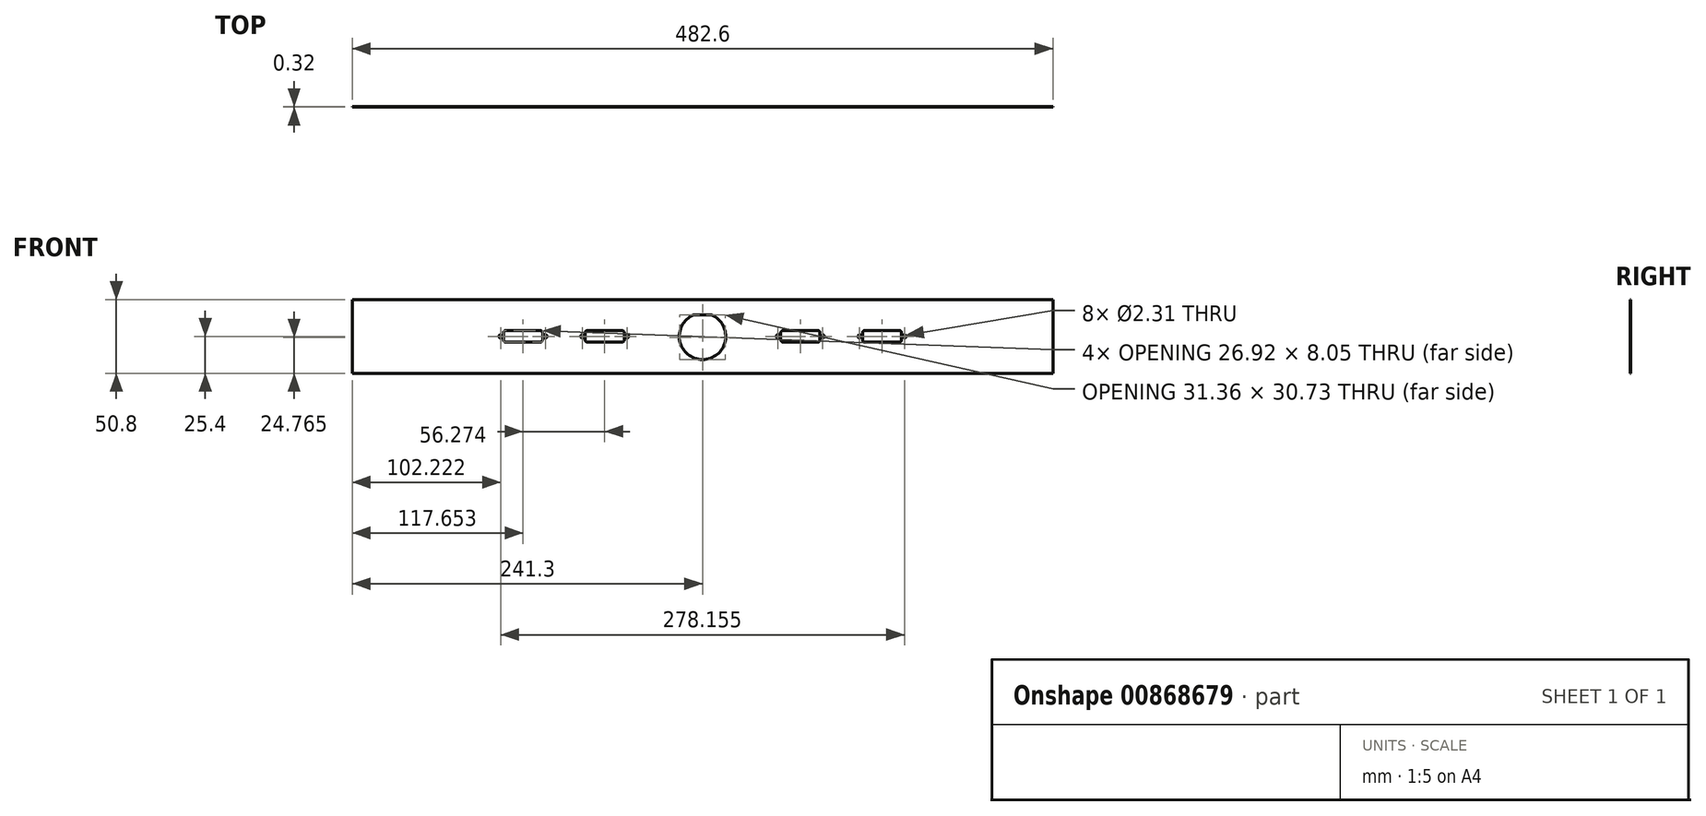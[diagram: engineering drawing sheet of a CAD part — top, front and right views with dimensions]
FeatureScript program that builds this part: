
annotation { "Feature Type Name" : "Feature", "Feature Type Description" : "" }
export const myFeature = defineFeature(function(context is Context, id is Id, definition is map)
    precondition{}
    {
        {
            var Q0;
            Q0=qCreatedBy(makeId("Front.planeOp"),FACE);
            var sketch = newSketch(context, id + "F0", { "sketchPlane" : qUnion([Q0])});
            skLineSegment(sketch, "E0.bottom", {"start": v(-241.3, 25.4) * mm, "end": v(241.3, 25.4) * mm});
            skLineSegment(sketch, "E0.top", {"start": v(-241.3, -25.4) * mm, "end": v(241.3, -25.4) * mm});
            skLineSegment(sketch, "E0.left", {"start": v(-241.3, 25.4) * mm, "end": v(-241.3, -25.4) * mm});
            skLineSegment(sketch, "E0.right", {"start": v(241.3, 25.4) * mm, "end": v(241.3, -25.4) * mm});
            skPoint(sketch, "E0.middle", {"position": v(0, 0) * mm});
            skLineSegment(sketch, "E1.bottom", {"start": v(-111.76, -4.03) * mm, "end": v(-135.53, -4.03) * mm});
            skLineSegment(sketch, "E1.top", {"start": v(-111.76, 4.03) * mm, "end": v(-135.53, 4.03) * mm});
            skLineSegment(sketch, "E1.left", {"start": v(-110.19, -2.45) * mm, "end": v(-110.19, 2.45) * mm});
            skLineSegment(sketch, "E1.right", {"start": v(-137.1, -2.45) * mm, "end": v(-137.1, 2.45) * mm});
            skPoint(sketch, "E1.middle", {"position": v(-123.65, 0) * mm});
            skPoint(sketch, "E2", {"position": v(-139.08, 0) * mm});
            skPoint(sketch, "E3", {"position": v(-108.22, 0) * mm});
            skPoint(sketch, "E4.visualSharp", {"position": v(-137.1, 4.03) * mm});
            skArc(sketch, "E4.filletArc", {"start": v(-135.53, 4.03) * mm, "mid": v(-136.65, 3.56) * mm, "end": v(-137.1, 2.45) * mm});
            skPoint(sketch, "E5.visualSharp", {"position": v(-137.1, -4.03) * mm});
            skArc(sketch, "E5.filletArc", {"start": v(-137.1, -2.45) * mm, "mid": v(-136.65, -3.56) * mm, "end": v(-135.53, -4.03) * mm});
            skPoint(sketch, "E6.visualSharp", {"position": v(-110.19, 4.03) * mm});
            skArc(sketch, "E6.filletArc", {"start": v(-110.19, 2.45) * mm, "mid": v(-110.65, 3.56) * mm, "end": v(-111.76, 4.03) * mm});
            skPoint(sketch, "E7.visualSharp", {"position": v(-110.19, -4.03) * mm});
            skArc(sketch, "E7.filletArc", {"start": v(-111.76, -4.03) * mm, "mid": v(-110.65, -3.56) * mm, "end": v(-110.19, -2.45) * mm});
            skCircle(sketch, "E8", {"center": v(-139.08, 0) * mm, "radius": 1.16 * mm});
            skCircle(sketch, "E9", {"center": v(-108.22, 0) * mm, "radius": 1.16 * mm});
            skLineSegment(sketch, "E10.bottom", {"start": v(-55.49, 4.03) * mm, "end": v(-79.26, 4.03) * mm});
            skLineSegment(sketch, "E10.top", {"start": v(-55.49, -4.03) * mm, "end": v(-79.26, -4.03) * mm});
            skLineSegment(sketch, "E10.left", {"start": v(-53.91, 2.45) * mm, "end": v(-53.91, -2.45) * mm});
            skLineSegment(sketch, "E10.right", {"start": v(-80.84, 2.45) * mm, "end": v(-80.84, -2.45) * mm});
            skPoint(sketch, "E10.middle", {"position": v(-67.37, 0) * mm});
            skCircle(sketch, "E11", {"center": v(-82.82, 0) * mm, "radius": 1.16 * mm});
            skCircle(sketch, "E12", {"center": v(-51.96, 0) * mm, "radius": 1.16 * mm});
            skPoint(sketch, "E13.visualSharp", {"position": v(-80.84, -4.03) * mm});
            skArc(sketch, "E13.filletArc", {"start": v(-80.84, -2.45) * mm, "mid": v(-80.37, -3.56) * mm, "end": v(-79.26, -4.03) * mm});
            skPoint(sketch, "E14.visualSharp", {"position": v(-80.84, 4.03) * mm});
            skArc(sketch, "E14.filletArc", {"start": v(-79.26, 4.03) * mm, "mid": v(-80.37, 3.56) * mm, "end": v(-80.84, 2.45) * mm});
            skPoint(sketch, "E15.visualSharp", {"position": v(-53.91, 4.03) * mm});
            skArc(sketch, "E15.filletArc", {"start": v(-53.91, 2.45) * mm, "mid": v(-54.37, 3.56) * mm, "end": v(-55.49, 4.03) * mm});
            skPoint(sketch, "E16.visualSharp", {"position": v(-53.91, -4.03) * mm});
            skArc(sketch, "E16.filletArc", {"start": v(-55.49, -4.03) * mm, "mid": v(-54.37, -3.56) * mm, "end": v(-53.91, -2.45) * mm});
            skLineSegment(sketch, "E17", {"start": v(0, 10.02) * mm, "end": v(0, -13.04) * mm});
            skCircle(sketch, "E18.MirrorC", {"center": v(108.22, 0) * mm, "radius": 1.16 * mm});
            skArc(sketch, "E19.MirrorCS", {"start": v(137.1, -2.45) * mm, "mid": v(136.65, -3.56) * mm, "end": v(135.53, -4.03) * mm});
            skArc(sketch, "E20.MirrorCS", {"start": v(53.91, 2.45) * mm, "mid": v(54.37, 3.56) * mm, "end": v(55.49, 4.03) * mm});
            skArc(sketch, "E21.MirrorCS", {"start": v(111.76, -4.03) * mm, "mid": v(110.65, -3.56) * mm, "end": v(110.19, -2.45) * mm});
            skLineSegment(sketch, "E22.MirrorCS", {"start": v(137.1, -2.45) * mm, "end": v(137.1, 2.45) * mm});
            skLineSegment(sketch, "E23.MirrorCS", {"start": v(53.91, 2.45) * mm, "end": v(53.91, -2.45) * mm});
            skArc(sketch, "E24.MirrorCS", {"start": v(135.53, 4.03) * mm, "mid": v(136.65, 3.56) * mm, "end": v(137.1, 2.45) * mm});
            skCircle(sketch, "E25.MirrorC", {"center": v(51.96, 0) * mm, "radius": 1.16 * mm});
            skArc(sketch, "E26.MirrorCS", {"start": v(80.84, -2.45) * mm, "mid": v(80.37, -3.56) * mm, "end": v(79.26, -4.03) * mm});
            skArc(sketch, "E27.MirrorCS", {"start": v(79.26, 4.03) * mm, "mid": v(80.37, 3.56) * mm, "end": v(80.84, 2.45) * mm});
            skLineSegment(sketch, "E28.MirrorCS", {"start": v(80.84, 2.45) * mm, "end": v(80.84, -2.45) * mm});
            skLineSegment(sketch, "E29.MirrorCS", {"start": v(110.19, -2.45) * mm, "end": v(110.19, 2.45) * mm});
            skArc(sketch, "E30.MirrorCS", {"start": v(55.49, -4.03) * mm, "mid": v(54.37, -3.56) * mm, "end": v(53.91, -2.45) * mm});
            skArc(sketch, "E31.MirrorCS", {"start": v(110.19, 2.45) * mm, "mid": v(110.65, 3.56) * mm, "end": v(111.76, 4.03) * mm});
            skCircle(sketch, "E32.MirrorC", {"center": v(139.08, 0) * mm, "radius": 1.16 * mm});
            skCircle(sketch, "E33.MirrorC", {"center": v(82.82, 0) * mm, "radius": 1.16 * mm});
            skLineSegment(sketch, "E34.MirrorCS", {"start": v(55.49, -4.03) * mm, "end": v(79.26, -4.03) * mm});
            skLineSegment(sketch, "E35.MirrorCS", {"start": v(111.76, 4.03) * mm, "end": v(135.53, 4.03) * mm});
            skLineSegment(sketch, "E36.MirrorCS", {"start": v(55.49, 4.03) * mm, "end": v(79.26, 4.03) * mm});
            skLineSegment(sketch, "E37.MirrorCS", {"start": v(111.76, -4.03) * mm, "end": v(135.53, -4.03) * mm});
            skPoint(sketch, "E38.MirrorP", {"position": v(137.1, 4.03) * mm});
            skPoint(sketch, "E39.MirrorP", {"position": v(110.19, 4.03) * mm});
            skPoint(sketch, "E40.MirrorP", {"position": v(80.84, 4.03) * mm});
            skPoint(sketch, "E41.MirrorP", {"position": v(123.65, 0) * mm});
            skPoint(sketch, "E42.MirrorP", {"position": v(137.1, -4.03) * mm});
            skPoint(sketch, "E43.MirrorP", {"position": v(53.91, 4.03) * mm});
            skPoint(sketch, "E44.MirrorP", {"position": v(67.37, 0) * mm});
            skPoint(sketch, "E45.MirrorP", {"position": v(80.84, -4.03) * mm});
            skPoint(sketch, "E46.MirrorP", {"position": v(110.19, -4.03) * mm});
            skPoint(sketch, "E47.MirrorP", {"position": v(53.91, -4.03) * mm});
            skArc(sketch, "E48", {"start": v(-6.25, 14.73) * mm, "mid": v(0, -16) * mm, "end": v(6.25, 14.73) * mm});
            skLineSegment(sketch, "E49", {"start": v(-6.25, 14.73) * mm, "end": v(6.25, 14.73) * mm});
            skSolve(sketch);
        }
        {
            var Q0;
            Q0=makeQuery(id+"F0.imprint","IMPRINT",FACE,{"disambiguationData":[TD([[makeQuery(id+"F0.imprint","IMPRINT",EDGE,{"derivedFrom":sQuery(id+"F0.wireOp",EDGE,"E0.bottom")}),-1.0]])]});
            extrude(context, id + "F1", {"entities" : qUnion([Q0]), "depth" : 0.32 * mm, "offsetDistance" : 25.4 * mm});
        }
    });
